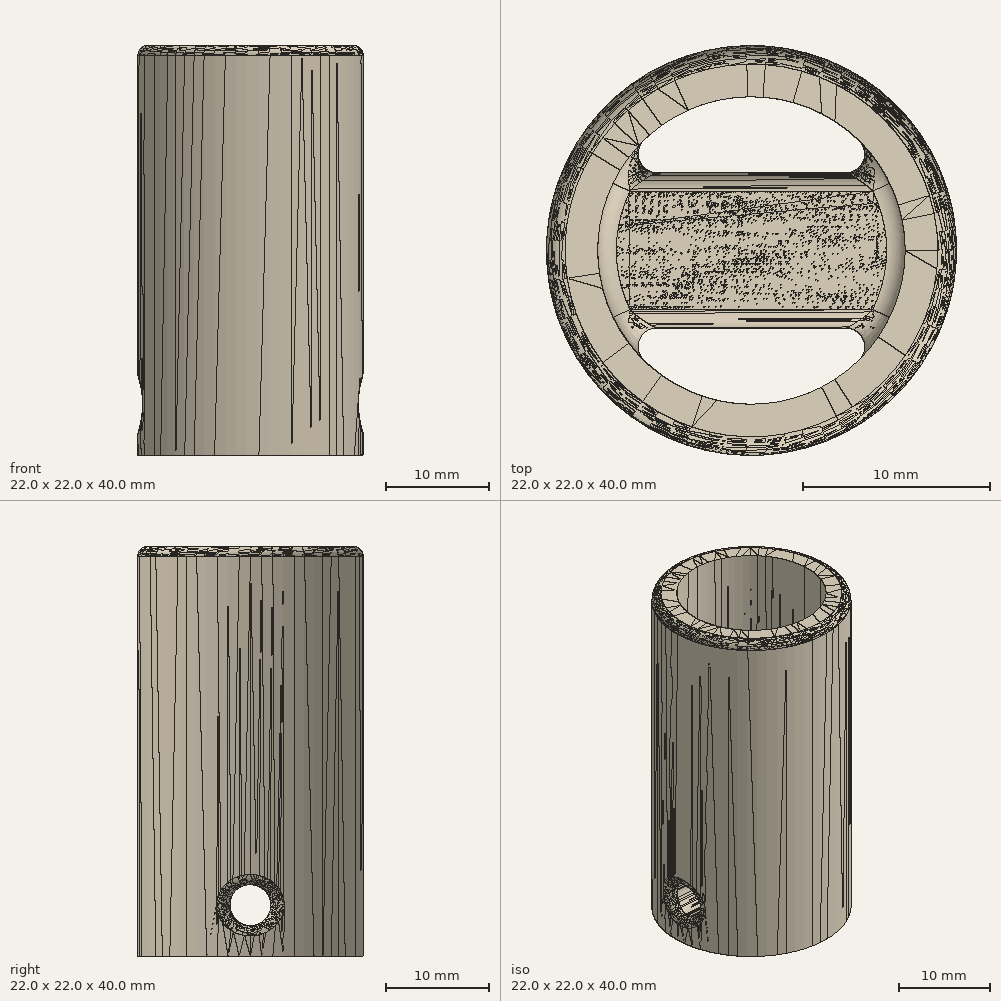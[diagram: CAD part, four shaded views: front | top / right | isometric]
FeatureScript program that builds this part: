
annotation { "Feature Type Name" : "Feature", "Feature Type Description" : "" }
export const myFeature = defineFeature(function(context is Context, id is Id, definition is map)
    precondition{}
    {
        {
            var Q0;
            Q0=qCreatedBy(makeId("Top.planeOp"),FACE);
            var sketch = newSketch(context, id + "F0", { "sketchPlane" : qUnion([Q0])});
            skCircle(sketch, "E0", {"center": v(0, 0) * mm, "radius": 11 * mm});
            skSolve(sketch);
        }
        {
            var Q0;
            Q0 = qSketchRegion(id + "F0", true);
            extrude(context, id + "F1", {"entities" : qUnion([Q0]), "depth" : 40 * mm});
        }
        {
            var Q0;
            Q0=makeQuery(id+"F1.opExtrude","CAP_FACE",FACE,{"disambiguationData":[OSD([sQuery(id+"F0.wireOp",EDGE,"E0")])],"isStart":false});
            var sketch = newSketch(context, id + "F2", { "sketchPlane" : qUnion([Q0])});
            skCircle(sketch, "E1", {"center": v(0, 0) * mm, "radius": 8.25 * mm});
            skSolve(sketch);
        }
        {
            var Q0;
            Q0=makeQuery(id+"F2.imprint","IMPRINT",FACE,{"disambiguationData":[TD([[makeQuery(id+"F2.imprint","IMPRINT",EDGE,{"derivedFrom":sQuery(id+"F2.wireOp",EDGE,"E1")}),1.0]])]});
            extrude(context, id + "F3", {"entities" : qUnion([Q0]), "operationType" : NewBodyOperationType.REMOVE, "oppositeDirection" : true, "depth" : 29.26 * mm});
        }
        {
            var Q0;
            Q0=qCreatedBy(makeId("Right.planeOp"),FACE);
            var sketch = newSketch(context, id + "F4", { "sketchPlane" : qUnion([Q0])});
            skCircle(sketch, "E2", {"center": v(0, 5) * mm, "radius": 2 * mm});
            skSolve(sketch);
        }
        {
            var Q0;
            Q0 = qSketchRegion(id + "F4", true);
            extrude(context, id + "F5", {"entities" : qUnion([Q0]), "operationType" : NewBodyOperationType.REMOVE, "oppositeDirection" : true, "depth" : 48.26 * mm, "symmetric" : true});
        }
        {
            var Q0;
            Q0=makeQuery(id+"F1.opExtrude","CAP_FACE",FACE,{"disambiguationData":[OSD([sQuery(id+"F0.wireOp",EDGE,"E0")])],"isStart":true});
            var sketch = newSketch(context, id + "F6", { "sketchPlane" : qUnion([Q0])});
            skCircle(sketch, "E3", {"center": v(0, 0) * mm, "radius": 8.25 * mm});
            skLineSegment(sketch, "E4", {"start": v(7.12, 4.17) * mm, "end": v(-7.12, 4.17) * mm});
            skLineSegment(sketch, "E5", {"start": v(7.12, -4.17) * mm, "end": v(-7.12, -4.17) * mm});
            skLineSegment(sketch, "E6", {"start": v(8.25, 0) * mm, "end": v(0, 0) * mm, "construction": true});
            skSolve(sketch);
        }
        {
            var Q0;
            {var subQ0=sQuery(id+"F6.wireOp",EDGE,"E4");Q0=makeQuery(id+"F6.imprint","IMPRINT",FACE,{"disambiguationData":[TD([[makeQuery(id+"F6.imprint","IMPRINT",EDGE,{"derivedFrom":subQ0}),-1.0]])]});}
            var Q1;
            {var subQ0=sQuery(id+"F6.wireOp",EDGE,"E5");Q1=makeQuery(id+"F6.imprint","IMPRINT",FACE,{"disambiguationData":[TD([[makeQuery(id+"F6.imprint","IMPRINT",EDGE,{"derivedFrom":subQ0}),1.0]])]});}
            extrude(context, id + "F7", {"entities" : qUnion([Q0, Q1]), "operationType" : NewBodyOperationType.REMOVE, "oppositeDirection" : true, "depth" : 36.5 * mm});
        }
        {
            var Q0;
            Q0=makeQuery(id+"F1.opExtrude","CAP_EDGE",EDGE,{"disambiguationData":[OSD([sQuery(id+"F0.wireOp",EDGE,"E0")])],"isStart":false});
            var Q1;
            Q1=makeQuery(id+"F3.boolean.opBoolean","COPY",EDGE,{"derivedFrom":makeQuery(id+"F3.opExtrude","CAP_EDGE",EDGE,{"disambiguationData":[OSD([sQuery(id+"F2.wireOp",EDGE,"E1")])],"isStart":true})});
            fillet(context, id + "F8", {"entities" : qUnion([Q0, Q1]), "radius" : 1 * mm, "allowEdgeOverflow" : false});
        }
        {
            var Q0;
            Q0=makeQuery(id+"F7.boolean.opBoolean","SPLIT",EDGE,{"disambiguationData":[OD(0.0)],"derivedFrom":makeQuery(id+"F3.boolean.opBoolean","COPY",EDGE,{"derivedFrom":makeQuery(id+"F3.opExtrude","CAP_EDGE",EDGE,{"disambiguationData":[OSD([sQuery(id+"F2.wireOp",EDGE,"E1")])],"isStart":false})})});
            var Q1;
            Q1=makeQuery(id+"F7.boolean.opBoolean","SPLIT",EDGE,{"disambiguationData":[OD(1.0)],"derivedFrom":makeQuery(id+"F3.boolean.opBoolean","COPY",EDGE,{"derivedFrom":makeQuery(id+"F3.opExtrude","CAP_EDGE",EDGE,{"disambiguationData":[OSD([sQuery(id+"F2.wireOp",EDGE,"E1")])],"isStart":false})})});
            var Q2;
            Q2=makeQuery(id+"F7.boolean.opBoolean","COPY",EDGE,{"derivedFrom":makeQuery(id+"F7.opExtrude","CAP_EDGE",EDGE,{"disambiguationData":[OSD([sQuery(id+"F6.wireOp",EDGE,"E5")])],"isStart":true})});
            var Q3;
            Q3=makeQuery(id+"F7.boolean.opBoolean","COPY",EDGE,{"derivedFrom":makeQuery(id+"F7.opExtrude","CAP_EDGE",EDGE,{"disambiguationData":[OSD([sQuery(id+"F6.wireOp",EDGE,"E4")])],"isStart":true})});
            var Q4;
            {var subQ0=sQuery(id+"F6.wireOp",EDGE,"E3");var subQ1=sQuery(id+"F6.wireOp",EDGE,"E5");Q4=makeQuery(id+"F7.boolean.opBoolean","COPY",EDGE,{"derivedFrom":makeQuery(id+"F7.opExtrude","SWEPT_EDGE",EDGE,{"disambiguationData":[OSD([subQ0,subQ1]),TDD([makeQuery(id+"F6.imprint","INTERSECT",VERTEX,{"disambiguationData":[OD(1.0)],"derivedFrom":[subQ0,subQ1]})])]})});}
            var Q5;
            {var subQ0=sQuery(id+"F6.wireOp",EDGE,"E3");var subQ1=sQuery(id+"F6.wireOp",EDGE,"E5");Q5=makeQuery(id+"F7.boolean.opBoolean","COPY",EDGE,{"derivedFrom":makeQuery(id+"F7.opExtrude","SWEPT_EDGE",EDGE,{"disambiguationData":[OSD([subQ0,subQ1]),TDD([makeQuery(id+"F6.imprint","INTERSECT",VERTEX,{"disambiguationData":[OD(0.0)],"derivedFrom":[subQ0,subQ1]})])]})});}
            var Q6;
            Q6=makeQuery(id+"F7.boolean.opBoolean","COPY",FACE,{"derivedFrom":makeQuery(id+"F7.opExtrude","SWEPT_FACE",FACE,{"disambiguationData":[OSD([sQuery(id+"F6.wireOp",EDGE,"E4")])]})});
            var Q7;
            Q7=makeQuery(id+"F7.boolean.opBoolean","INTERSECT",EDGE,{"derivedFrom":[makeQuery(id+"F3.boolean.opBoolean","COPY",FACE,{"derivedFrom":makeQuery(id+"F3.opExtrude","CAP_FACE",FACE,{"disambiguationData":[OSD([sQuery(id+"F2.wireOp",EDGE,"E1")])],"isStart":false})}),makeQuery(id+"F7.opExtrude","SWEPT_FACE",FACE,{"disambiguationData":[OSD([sQuery(id+"F6.wireOp",EDGE,"E5")])]})]});
            var Q8;
            Q8=makeQuery(id+"F5.boolean.opBoolean","INTERSECT",EDGE,{"disambiguationData":[OD(0.0)],"derivedFrom":[makeQuery(id+"F1.opExtrude","SWEPT_FACE",FACE,{"disambiguationData":[OSD([sQuery(id+"F0.wireOp",EDGE,"E0")])]}),makeQuery(id+"F5.opExtrude","SWEPT_FACE",FACE,{"disambiguationData":[OSD([sQuery(id+"F4.wireOp",EDGE,"E2")])]})]});
            var Q9;
            Q9=makeQuery(id+"F5.boolean.opBoolean","INTERSECT",EDGE,{"disambiguationData":[OD(1.0)],"derivedFrom":[makeQuery(id+"F1.opExtrude","SWEPT_FACE",FACE,{"disambiguationData":[OSD([sQuery(id+"F0.wireOp",EDGE,"E0")])]}),makeQuery(id+"F5.opExtrude","SWEPT_FACE",FACE,{"disambiguationData":[OSD([sQuery(id+"F4.wireOp",EDGE,"E2")])]})]});
            fillet(context, id + "F9", {"entities" : qUnion([Q0, Q1, Q2, Q3, Q4, Q5, Q6, Q7, Q8, Q9]), "radius" : 1 * mm, "tangentPropagation" : true, "allowEdgeOverflow" : false});
        }
    });
